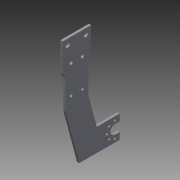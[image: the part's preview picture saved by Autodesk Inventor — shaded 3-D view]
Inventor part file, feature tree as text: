
AUTODESK INVENTOR PART (.ipt)
format: ipt  version: 2013 (Build 170138000, 138)  size: 173,056 bytes
history: native  units: mm
features: sketch x5, extrude x3, hole x2, other x1, pattern_circular x1
ambient origin geometry x8: Origin, YZ Plane, XZ Plane, XY Plane, X Axis, Y Axis, Z Axis, Center Point
feature tree (12):
  other  "ソリッド1"
  extrude  "押し出し1"  Depth=50.0mm
  extrude  "押し出し2"  Depth=100.0mm
  extrude  "押し出し5"  Depth=50.0mm
  hole  "穴1"  [1 undecoded]
  pattern_circular  "円形状パターン2"  [2 undecoded]
  hole  "穴2"  [1 undecoded]
  sketch  "スケッチ1"
  sketch  "スケッチ2"
  sketch  "スケッチ3"
  sketch  "スケッチ4"
  sketch  "スケッチ5"
note: 4 required parameter values undecoded (feature->parameter linkage not recoverable at this tier; creation-order binding heuristic only, values carry confidence <= 0.55)
